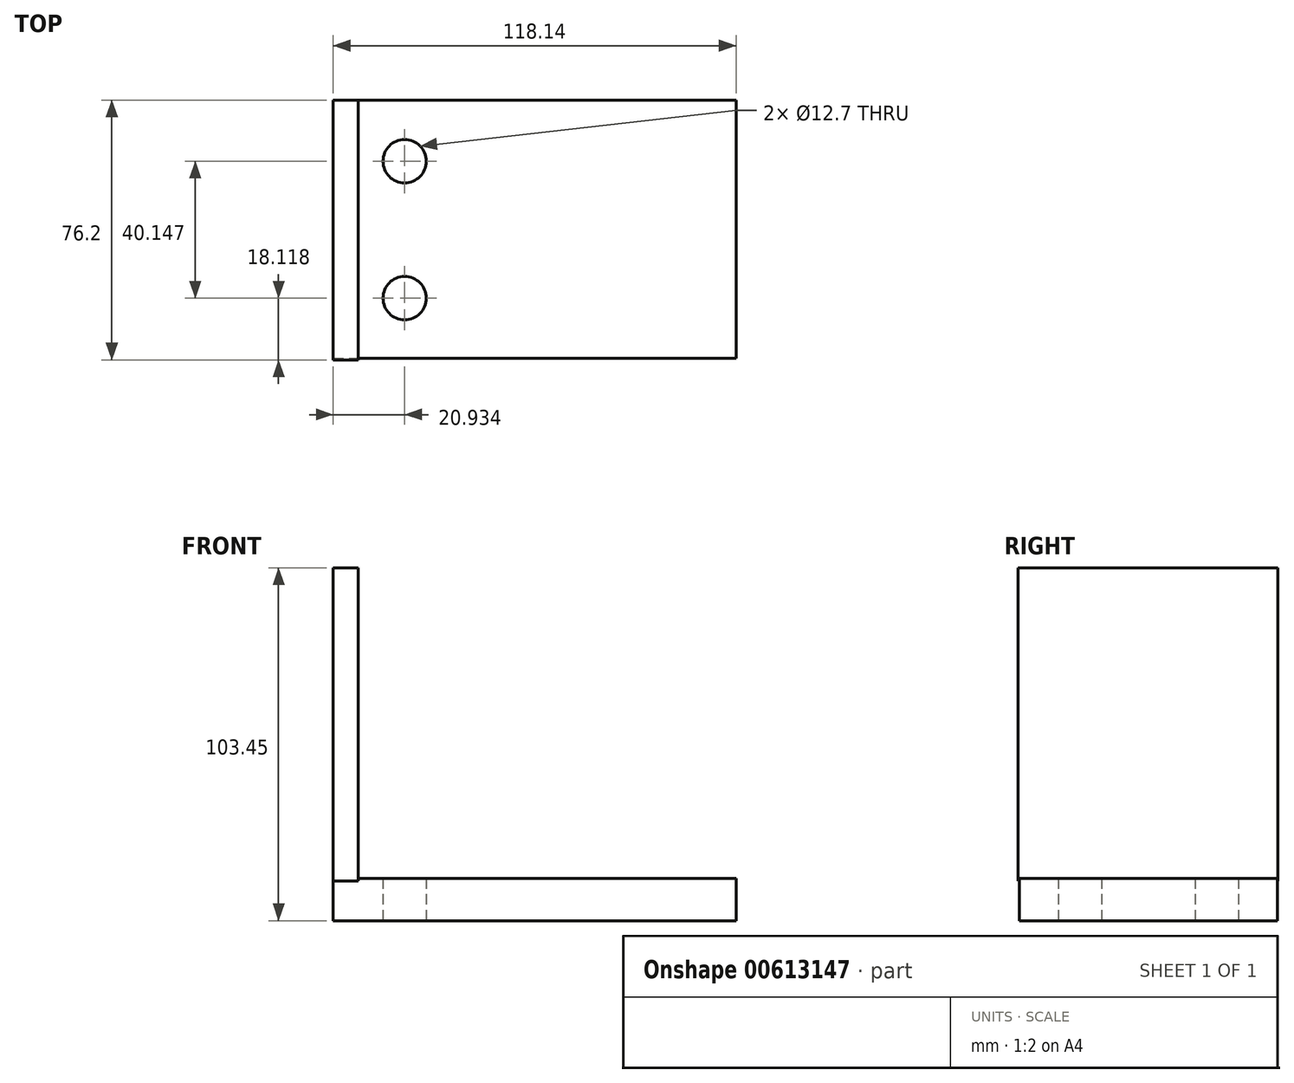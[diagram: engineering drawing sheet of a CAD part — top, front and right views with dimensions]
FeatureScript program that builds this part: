
annotation { "Feature Type Name" : "Feature", "Feature Type Description" : "" }
export const myFeature = defineFeature(function(context is Context, id is Id, definition is map)
    precondition{}
    {
        {
            var Q0;
            Q0=qCreatedBy(makeId("Right.planeOp"),FACE);
            var sketch = newSketch(context, id + "F0", { "sketchPlane" : qUnion([Q0])});
            skLineSegment(sketch, "E0.bottom", {"start": v(-35.22, 47.47) * mm, "end": v(40.98, 47.47) * mm});
            skLineSegment(sketch, "E0.top", {"start": v(-35.22, -44.3) * mm, "end": v(40.98, -44.3) * mm});
            skLineSegment(sketch, "E0.left", {"start": v(-35.22, 47.47) * mm, "end": v(-35.22, -44.3) * mm});
            skLineSegment(sketch, "E0.right", {"start": v(40.98, 47.47) * mm, "end": v(40.98, -44.3) * mm});
            skSolve(sketch);
        }
        {
            var Q0;
            Q0 = qSketchRegion(id + "F0", true);
            extrude(context, id + "F1", {"entities" : qUnion([Q0]), "depth" : 7.37 * mm, "offsetDistance" : 25.4 * mm});
        }
        {
            var Q0;
            Q0=qCreatedBy(makeId("Front.planeOp"),FACE);
            var sketch = newSketch(context, id + "F2", { "sketchPlane" : qUnion([Q0])});
            skLineSegment(sketch, "E1.bottom", {"start": v(0, -43.6) * mm, "end": v(118.14, -43.6) * mm});
            skLineSegment(sketch, "E1.top", {"start": v(0, -55.98) * mm, "end": v(118.14, -55.98) * mm});
            skLineSegment(sketch, "E1.left", {"start": v(0, -43.6) * mm, "end": v(0, -55.98) * mm});
            skLineSegment(sketch, "E1.right", {"start": v(118.14, -43.6) * mm, "end": v(118.14, -55.98) * mm});
            skSolve(sketch);
        }
        {
            var Q0;
            Q0 = qSketchRegion(id + "F2", true);
            extrude(context, id + "F3", {"entities" : qUnion([Q0]), "operationType" : NewBodyOperationType.ADD, "depth" : 34.8 * mm, "offsetDistance" : 25.4 * mm});
        }
        {
            var Q0;
            Q0 = qSketchRegion(id + "F2", true);
            extrude(context, id + "F4", {"entities" : qUnion([Q0]), "operationType" : NewBodyOperationType.ADD, "oppositeDirection" : true, "depth" : 40.9 * mm, "offsetDistance" : 25.4 * mm});
        }
        {
            var Q0;
            {var subQ0=sQuery(id+"F2.wireOp",EDGE,"E1.top");Q0=makeQuery(id+"F4.boolean.opBoolean","MERGE",FACE,{"derivedFrom":[makeQuery(id+"F3.opExtrude","SWEPT_FACE",FACE,{"disambiguationData":[OSD([subQ0])]}),makeQuery(id+"F4.opExtrude","SWEPT_FACE",FACE,{"disambiguationData":[OSD([subQ0])]})]});}
            var sketch = newSketch(context, id + "F5", { "sketchPlane" : qUnion([Q0])});
            skCircle(sketch, "E2", {"center": v(20.93, -23.05) * mm, "radius": 6.35 * mm});
            skCircle(sketch, "E3", {"center": v(20.93, 17.1) * mm, "radius": 6.35 * mm});
            skSolve(sketch);
        }
        {
            var Q0;
            Q0 = qSketchRegion(id + "F5", true);
            extrude(context, id + "F6", {"entities" : qUnion([Q0]), "operationType" : NewBodyOperationType.REMOVE, "oppositeDirection" : true, "depth" : 25.4 * mm, "offsetDistance" : 25.4 * mm});
        }
    });
